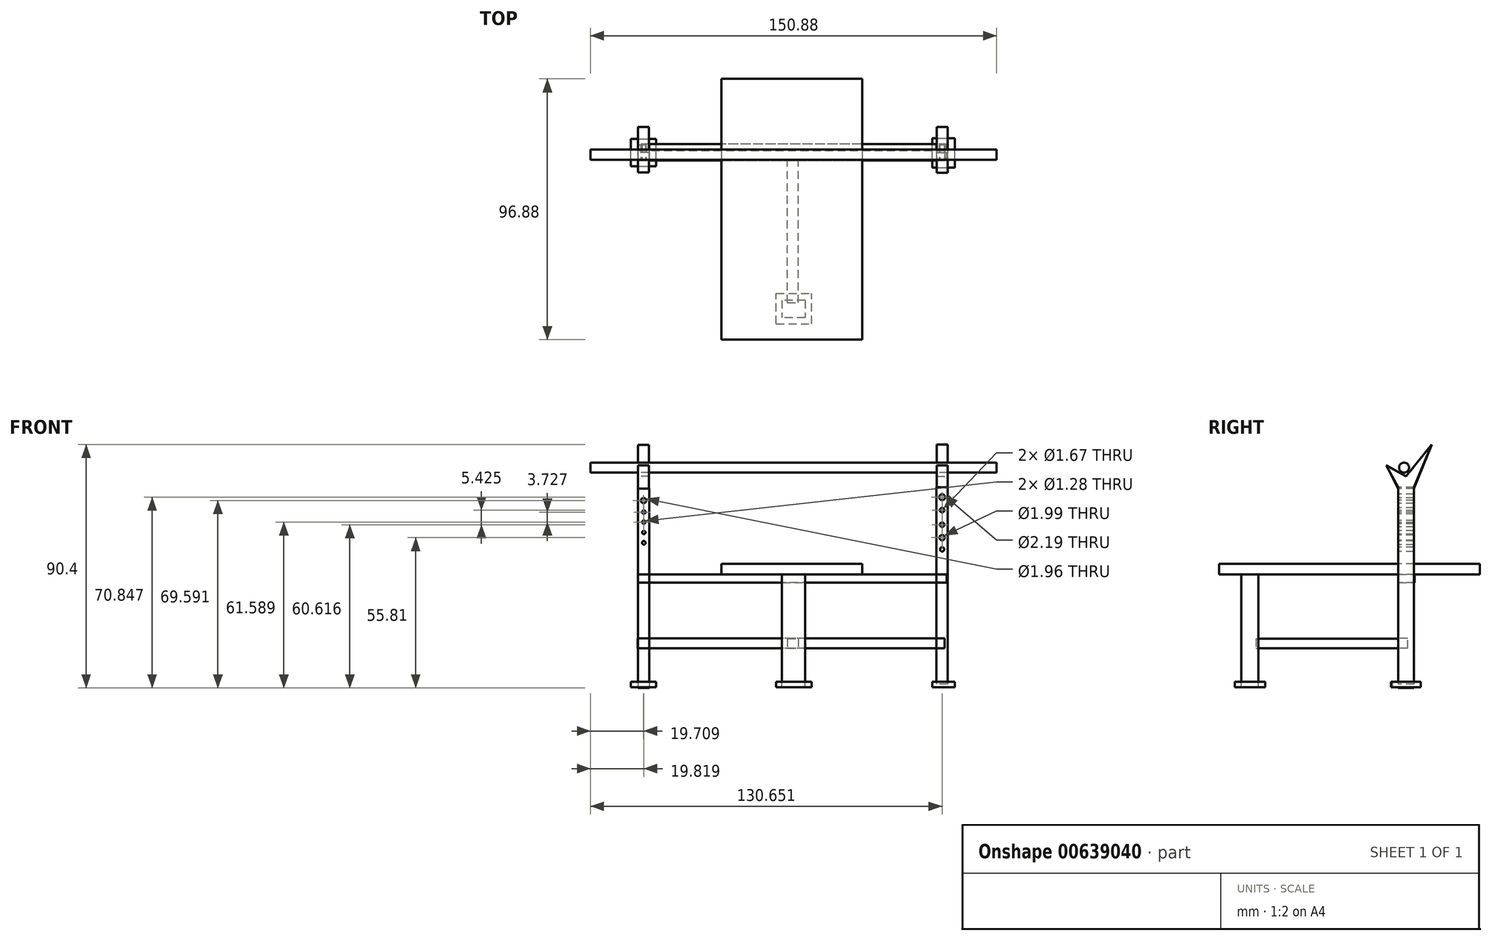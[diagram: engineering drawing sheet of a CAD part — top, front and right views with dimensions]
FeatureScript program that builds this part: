
annotation { "Feature Type Name" : "Feature", "Feature Type Description" : "" }
export const myFeature = defineFeature(function(context is Context, id is Id, definition is map)
    precondition{}
    {
        {
            var Q0;
            Q0=qCreatedBy(makeId("Top.planeOp"),FACE);
            var sketch = newSketch(context, id + "F0", { "sketchPlane" : qUnion([Q0])});
            skLineSegment(sketch, "E0.bottom", {"start": v(-26.84, 30.33) * mm, "end": v(25.53, 30.33) * mm});
            skLineSegment(sketch, "E0.top", {"start": v(-26.84, -66.55) * mm, "end": v(25.53, -66.55) * mm});
            skLineSegment(sketch, "E0.left", {"start": v(-26.84, 30.33) * mm, "end": v(-26.84, -66.55) * mm});
            skLineSegment(sketch, "E0.right", {"start": v(25.53, 30.33) * mm, "end": v(25.53, -66.55) * mm});
            skSolve(sketch);
        }
        {
            var Q0;
            Q0 = qSketchRegion(id + "F0", true);
            extrude(context, id + "F1", {"entities" : qUnion([Q0]), "depth" : 4 * mm, "offsetDistance" : 25.4 * mm});
        }
        {
            var Q0;
            Q0=makeQuery(id+"F1.opExtrude","CAP_FACE",FACE,{"disambiguationData":[OSD([sQuery(id+"F0.wireOp",EDGE,"E0.bottom"),sQuery(id+"F0.wireOp",EDGE,"E0.top"),sQuery(id+"F0.wireOp",EDGE,"E0.left"),sQuery(id+"F0.wireOp",EDGE,"E0.right")])],"isStart":true});
            var sketch = newSketch(context, id + "F2", { "sketchPlane" : qUnion([Q0])});
            skLineSegment(sketch, "E1", {"start": v(56.95, -6.09) * mm, "end": v(-57.8, -6.09) * mm});
            skLineSegment(sketch, "E2", {"start": v(-57.8, -6.09) * mm, "end": v(-57.8, 0) * mm});
            skLineSegment(sketch, "E3", {"start": v(-57.8, 0) * mm, "end": v(56.95, 0) * mm});
            skLineSegment(sketch, "E4", {"start": v(56.95, 0) * mm, "end": v(56.95, -6.09) * mm});
            skSolve(sketch);
        }
        {
            var Q0;
            Q0 = qSketchRegion(id + "F2", true);
            extrude(context, id + "F3", {"entities" : qUnion([Q0]), "operationType" : NewBodyOperationType.ADD, "depth" : 3.05 * mm, "offsetDistance" : 25.4 * mm});
        }
        {
            var Q0;
            {var subQ0=sQuery(id+"F0.wireOp",EDGE,"E0.right");var subQ2=sQuery(id+"F0.wireOp",EDGE,"E0.left");var subQ3=sQuery(id+"F0.wireOp",EDGE,"E0.top");Q0=makeQuery(id+"F3.boolean.opBoolean","SPLIT",FACE,{"disambiguationData":[TD([makeQuery(id+"F1.opExtrude","SWEPT_FACE",FACE,{"disambiguationData":[OSD([subQ3])]})])],"derivedFrom":makeQuery(id+"F1.opExtrude","CAP_FACE",FACE,{"disambiguationData":[OSD([sQuery(id+"F0.wireOp",EDGE,"E0.bottom"),subQ3,subQ2,subQ0])],"isStart":true})});}
            var sketch = newSketch(context, id + "F4", { "sketchPlane" : qUnion([Q0])});
            skLineSegment(sketch, "E5.bottom", {"start": v(4.31, 51.95) * mm, "end": v(-4.28, 51.95) * mm});
            skLineSegment(sketch, "E5.top", {"start": v(4.31, 58.4) * mm, "end": v(-4.28, 58.4) * mm});
            skLineSegment(sketch, "E5.left", {"start": v(4.31, 51.95) * mm, "end": v(4.31, 58.4) * mm});
            skLineSegment(sketch, "E5.right", {"start": v(-4.28, 51.95) * mm, "end": v(-4.28, 58.4) * mm});
            skSolve(sketch);
        }
        {
            var Q0;
            Q0=makeQuery(id+"F4.imprint","IMPRINT",FACE,{"disambiguationData":[TD([[makeQuery(id+"F4.imprint","IMPRINT",EDGE,{"derivedFrom":sQuery(id+"F4.wireOp",EDGE,"E5.bottom")}),-1.0]])]});
            extrude(context, id + "F5", {"entities" : qUnion([Q0]), "operationType" : NewBodyOperationType.ADD, "depth" : 41.9 * mm, "offsetDistance" : 25.4 * mm});
        }
        {
            var Q0;
            Q0=qCreatedBy(makeId("Front.planeOp"),FACE);
            var sketch = newSketch(context, id + "F6", { "sketchPlane" : qUnion([Q0])});
            skLineSegment(sketch, "E6.bottom", {"start": v(56.13, -27.37) * mm, "end": v(-57.97, -27.37) * mm});
            skLineSegment(sketch, "E6.top", {"start": v(56.13, -23.7) * mm, "end": v(-57.97, -23.7) * mm});
            skLineSegment(sketch, "E6.left", {"start": v(56.13, -27.37) * mm, "end": v(56.13, -23.7) * mm});
            skLineSegment(sketch, "E6.right", {"start": v(-57.97, -27.37) * mm, "end": v(-57.97, -23.7) * mm});
            skSolve(sketch);
        }
        {
            var Q0;
            Q0=makeQuery(id+"F6.imprint","IMPRINT",FACE,{"disambiguationData":[TD([[makeQuery(id+"F6.imprint","IMPRINT",EDGE,{"derivedFrom":sQuery(id+"F6.wireOp",EDGE,"E6.bottom")}),-1.0]])]});
            extrude(context, id + "F7", {"entities" : qUnion([Q0]), "oppositeDirection" : true, "depth" : 3.56 * mm, "offsetDistance" : 25.4 * mm});
        }
        {
            var Q0;
            Q0=qCreatedBy(makeId("Front.planeOp"),FACE);
            var sketch = newSketch(context, id + "F8", { "sketchPlane" : qUnion([Q0])});
            skLineSegment(sketch, "E7.bottom", {"start": v(57.28, 32.43) * mm, "end": v(53.14, 32.43) * mm});
            skLineSegment(sketch, "E7.top", {"start": v(57.28, -40.71) * mm, "end": v(53.14, -40.71) * mm});
            skLineSegment(sketch, "E7.left", {"start": v(57.28, 32.43) * mm, "end": v(57.28, -40.71) * mm});
            skLineSegment(sketch, "E7.right", {"start": v(53.14, 32.43) * mm, "end": v(53.14, -40.71) * mm});
            skLineSegment(sketch, "E8.bottom", {"start": v(-57.74, 31.97) * mm, "end": v(-53.6, 31.97) * mm});
            skLineSegment(sketch, "E8.top", {"start": v(-57.74, -42.1) * mm, "end": v(-53.6, -42.1) * mm});
            skLineSegment(sketch, "E8.left", {"start": v(-57.74, 31.97) * mm, "end": v(-57.74, -42.1) * mm});
            skLineSegment(sketch, "E8.right", {"start": v(-53.6, 31.97) * mm, "end": v(-53.6, -42.1) * mm});
            skSolve(sketch);
        }
        {
            var Q0;
            Q0 = qSketchRegion(id + "F8", true);
            extrude(context, id + "F9", {"entities" : qUnion([Q0]), "oppositeDirection" : true, "depth" : 5.84 * mm, "offsetDistance" : 25.4 * mm});
        }
        {
            var Q0;
            Q0=makeQuery(id+"F7.opExtrude","SWEPT_FACE",FACE,{"disambiguationData":[OSD([sQuery(id+"F6.wireOp",EDGE,"E6.bottom")])]});
            var sketch = newSketch(context, id + "F10", { "sketchPlane" : qUnion([Q0])});
            skLineSegment(sketch, "E9.bottom", {"start": v(-2.28, 52.88) * mm, "end": v(1.82, 52.88) * mm});
            skLineSegment(sketch, "E9.top", {"start": v(-2.28, 0) * mm, "end": v(1.82, 0) * mm});
            skLineSegment(sketch, "E9.left", {"start": v(-2.28, 52.88) * mm, "end": v(-2.28, 0) * mm});
            skLineSegment(sketch, "E9.right", {"start": v(1.82, 52.88) * mm, "end": v(1.82, 0) * mm});
            skSolve(sketch);
        }
        {
            var Q0;
            Q0 = qSketchRegion(id + "F10", true);
            extrude(context, id + "F11", {"entities" : qUnion([Q0]), "oppositeDirection" : true, "depth" : 3.56 * mm, "offsetDistance" : 25.4 * mm});
        }
        {
            var Q0;
            Q0=makeQuery(id+"F9.opExtrude","SWEPT_FACE",FACE,{"disambiguationData":[OSD([sQuery(id+"F8.wireOp",EDGE,"E7.left")])]});
            var sketch = newSketch(context, id + "F12", { "sketchPlane" : qUnion([Q0])});
            skLineSegment(sketch, "E10", {"start": v(0, 32.43) * mm, "end": v(-4.52, 40.58) * mm});
            skLineSegment(sketch, "E11", {"start": v(-4.52, 40.58) * mm, "end": v(2.92, 36.5) * mm});
            skPoint(sketch, "E11.endSnap0", {"position": v(-2.26, 36.5) * mm});
            skPoint(sketch, "E11.endSnap1", {"position": v(2.92, 32.43) * mm});
            skLineSegment(sketch, "E12", {"start": v(2.92, 36.5) * mm, "end": v(12.45, 48.3) * mm});
            skLineSegment(sketch, "E13", {"start": v(12.45, 48.3) * mm, "end": v(5.84, 32.43) * mm});
            skLineSegment(sketch, "E14", {"start": v(5.84, 32.43) * mm, "end": v(0, 32.43) * mm});
            skSolve(sketch);
        }
        {
            var Q0;
            Q0=makeQuery(id+"F12.imprint","IMPRINT",FACE,{"disambiguationData":[TD([[makeQuery(id+"F12.imprint","IMPRINT",EDGE,{"derivedFrom":sQuery(id+"F12.wireOp",EDGE,"E10")}),-1.0]])]});
            extrude(context, id + "F13", {"entities" : qUnion([Q0]), "operationType" : NewBodyOperationType.ADD, "oppositeDirection" : true, "depth" : 4.06 * mm, "offsetDistance" : 25.4 * mm});
        }
        {
            var Q0;
            Q0=makeQuery(id+"F9.opExtrude","SWEPT_FACE",FACE,{"disambiguationData":[OSD([sQuery(id+"F8.wireOp",EDGE,"E8.left")])]});
            var sketch = newSketch(context, id + "F14", { "sketchPlane" : qUnion([Q0])});
            skLineSegment(sketch, "E15", {"start": v(-5.84, 31.97) * mm, "end": v(-12.44, 48.18) * mm});
            skLineSegment(sketch, "E16", {"start": v(-12.44, 48.18) * mm, "end": v(-2.91, 36.55) * mm});
            skLineSegment(sketch, "E17", {"start": v(-2.91, 36.55) * mm, "end": v(4.43, 40.57) * mm});
            skLineSegment(sketch, "E18", {"start": v(4.43, 40.57) * mm, "end": v(0, 31.97) * mm});
            skLineSegment(sketch, "E19", {"start": v(0, 31.97) * mm, "end": v(-5.84, 31.97) * mm});
            skSolve(sketch);
        }
        {
            var Q0;
            Q0=makeQuery(id+"F14.imprint","IMPRINT",FACE,{"disambiguationData":[TD([[makeQuery(id+"F14.imprint","IMPRINT",EDGE,{"derivedFrom":sQuery(id+"F14.wireOp",EDGE,"E15")}),-1.0]])]});
            extrude(context, id + "F15", {"entities" : qUnion([Q0]), "operationType" : NewBodyOperationType.ADD, "oppositeDirection" : true, "depth" : 4.06 * mm, "offsetDistance" : 25.4 * mm});
        }
        {
            var Q0;
            Q0=makeQuery(id+"F9.opExtrude","CAP_FACE",FACE,{"disambiguationData":[OSD([sQuery(id+"F8.wireOp",EDGE,"E8.bottom"),sQuery(id+"F8.wireOp",EDGE,"E8.top"),sQuery(id+"F8.wireOp",EDGE,"E8.left"),sQuery(id+"F8.wireOp",EDGE,"E8.right")])],"isStart":true});
            var sketch = newSketch(context, id + "F16", { "sketchPlane" : qUnion([Q0])});
            skCircle(sketch, "E20", {"center": v(-55.73, 27.5) * mm, "radius": 0.98 * mm});
            skCircle(sketch, "E21", {"center": v(-55.62, 23.22) * mm, "radius": 0.64 * mm});
            skCircle(sketch, "E22", {"center": v(-55.62, 19.49) * mm, "radius": 0.64 * mm});
            skCircle(sketch, "E23", {"center": v(-55.62, 15.65) * mm, "radius": 0.62 * mm});
            skCircle(sketch, "E24", {"center": v(-55.62, 11.82) * mm, "radius": 0.67 * mm});
            skSolve(sketch);
        }
        {
            var Q0;
            Q0 = qSketchRegion(id + "F16", true);
            extrude(context, id + "F17", {"entities" : qUnion([Q0]), "operationType" : NewBodyOperationType.REMOVE, "oppositeDirection" : true, "depth" : 25.4 * mm, "offsetDistance" : 25.4 * mm});
        }
        {
            var Q0;
            Q0=makeQuery(id+"F9.opExtrude","CAP_FACE",FACE,{"disambiguationData":[OSD([sQuery(id+"F8.wireOp",EDGE,"E7.bottom"),sQuery(id+"F8.wireOp",EDGE,"E7.top"),sQuery(id+"F8.wireOp",EDGE,"E7.left"),sQuery(id+"F8.wireOp",EDGE,"E7.right")])],"isStart":true});
            var sketch = newSketch(context, id + "F18", { "sketchPlane" : qUnion([Q0])});
            skCircle(sketch, "E25", {"center": v(55.21, 28.75) * mm, "radius": 1.1 * mm});
            skCircle(sketch, "E26", {"center": v(55.21, 23.94) * mm, "radius": 0.83 * mm});
            skCircle(sketch, "E27", {"center": v(55.21, 18.52) * mm, "radius": 0.83 * mm});
            skCircle(sketch, "E28", {"center": v(55.21, 13.71) * mm, "radius": 1 * mm});
            skCircle(sketch, "E29", {"center": v(55.21, 9.37) * mm, "radius": 0.8 * mm});
            skSolve(sketch);
        }
        {
            var Q0;
            Q0 = qSketchRegion(id + "F18", true);
            extrude(context, id + "F19", {"entities" : qUnion([Q0]), "operationType" : NewBodyOperationType.REMOVE, "oppositeDirection" : true, "depth" : 25.4 * mm, "offsetDistance" : 25.4 * mm});
        }
        {
            var Q0;
            Q0=makeQuery(id+"F5.opExtrude","CAP_FACE",FACE,{"disambiguationData":[OSD([sQuery(id+"F4.wireOp",EDGE,"E5.bottom"),sQuery(id+"F4.wireOp",EDGE,"E5.top"),sQuery(id+"F4.wireOp",EDGE,"E5.left"),sQuery(id+"F4.wireOp",EDGE,"E5.right")])],"isStart":false});
            var sketch = newSketch(context, id + "F20", { "sketchPlane" : qUnion([Q0])});
            skLineSegment(sketch, "E30.bottom", {"start": v(-6.43, 60.7) * mm, "end": v(6.72, 60.7) * mm});
            skLineSegment(sketch, "E30.top", {"start": v(-6.43, 49.43) * mm, "end": v(6.72, 49.43) * mm});
            skLineSegment(sketch, "E30.left", {"start": v(-6.43, 60.7) * mm, "end": v(-6.43, 49.43) * mm});
            skLineSegment(sketch, "E30.right", {"start": v(6.72, 60.7) * mm, "end": v(6.72, 49.43) * mm});
            skLineSegment(sketch, "E31.bottom", {"start": v(-60.4, 2.17) * mm, "end": v(-51, 2.17) * mm});
            skLineSegment(sketch, "E31.top", {"start": v(-60.4, -8.03) * mm, "end": v(-51, -8.03) * mm});
            skLineSegment(sketch, "E31.left", {"start": v(-60.4, 2.17) * mm, "end": v(-60.4, -8.03) * mm});
            skLineSegment(sketch, "E31.right", {"start": v(-51, 2.17) * mm, "end": v(-51, -8.03) * mm});
            skLineSegment(sketch, "E32.bottom", {"start": v(51.56, 2.71) * mm, "end": v(59.88, 2.71) * mm});
            skLineSegment(sketch, "E32.top", {"start": v(51.56, -8.3) * mm, "end": v(59.88, -8.3) * mm});
            skLineSegment(sketch, "E32.left", {"start": v(51.56, 2.71) * mm, "end": v(51.56, -8.3) * mm});
            skLineSegment(sketch, "E32.right", {"start": v(59.88, 2.71) * mm, "end": v(59.88, -8.3) * mm});
            skSolve(sketch);
        }
        {
            var Q0;
            Q0 = qSketchRegion(id + "F20", true);
            extrude(context, id + "F21", {"entities" : qUnion([Q0]), "oppositeDirection" : true, "depth" : 2.03 * mm, "offsetDistance" : 25.4 * mm});
        }
        {
            var Q0;
            Q0=qCreatedBy(makeId("Right.planeOp"),FACE);
            var sketch = newSketch(context, id + "F22", { "sketchPlane" : qUnion([Q0])});
            skCircle(sketch, "E33", {"center": v(2.15, 39.74) * mm, "radius": 1.86 * mm});
            skSolve(sketch);
        }
        {
            var Q0;
            Q0 = qSketchRegion(id + "F22", true);
            extrude(context, id + "F23", {"entities" : qUnion([Q0]), "operationType" : NewBodyOperationType.ADD, "endBound" : BoundingType.SYMMETRIC, "depth" : 150.88 * mm, "offsetDistance" : 25.4 * mm});
        }
    });
